# Revit family: QF_Friginox_MX 75-35 A TS7
name_source: partatom
category: Specialty Equipment
units: mm (PartAtom-declared; Revit-internal decimal feet)

## family parameters
Always vertical = Yes
Cut with Voids When Loaded = No
Part Type = Normal
Room Calculation Point = No
Round Connector Dimension = Use Diameter
Shared = No
Work Plane-Based = No

## types (1)
- MX 75-35 A TS7
    Accessory = No
    CE Approved = Yes
    Condensate Return Connection Height = 580 mm  [stored 1.90289 ft]
    Condensate Return Size = 0 mm
    Conn Plug = Only cable
    Cost = 0 $
    Cycle = 50 Hz
    D15 = 15 mm  [stored 0.0492126 ft]
    Default Elevation = 0 mm  [stored 0 ft]
    Depth Actual = 820 mm  [stored 2.69029 ft]
    Description = Blast Chiller/Freezer, Reach-in GN1/1, 15 levels, Chill 75 kg
    Door_Depth = 135 mm  [stored 0.442913 ft]
    Door_W = 623 mm  [stored 2.04396 ft]
    Elec Connection Height = 190 mm  [stored 0.62336 ft]
    Electric power = 4000 W
    FL Amps = 0 A
    Foodservice Equipment Identifier = Yes
    Groupe frigorifique = Logé
    Height Actual = 1925 mm  [stored 6.31562 ft]
    Identify Quantity as Lot = No
    Item Number = FX39272623
    Keynote = 0
    Legs_R1 = 30 mm  [stored 0.0984252 ft]
    Legs_R2 = 25 mm  [stored 0.082021 ft]
    Length Actual = 770 mm  [stored 2.52625 ft]
    Main switch integrated = No
    Manufacturer = FRIGINOX
    Mat_Case = QF_Stainless-Brushed
    Mat_Clearance = QF_Clearance
    Mat_Legs = QF_Stainless-Brushed
    Model = MX 75-35 A TS7
    Number of Poles = 3
    Phase = 3
    Potential Equalisation = Yes
    Refrigerant Compressor Remote = No
    Refrigerant Mass = 0
    Refrigerant Volume = 0.0 L/s
    Refrigeration Defrost Drain = Yes
    Refrigeration Liquid Line Size = 0 mm
    Refrigeration Suction Line Size = 0 mm
    URL Cutsheet = FTEC_MX75-35ATS7_FR_0922.pdf
    URL Manufacturer = http://www.friginox.com
    Volt Free Conn = No
    Volts = 400 V
    Weight = 175.00 kg

note: [stored X ft] marks values corroborated as IEEE doubles in the binary element streams (Revit-internal decimal feet)

## geometry (parser evidence)
native form markers: Sweep x14
no freeform markers — native parametric forms only
